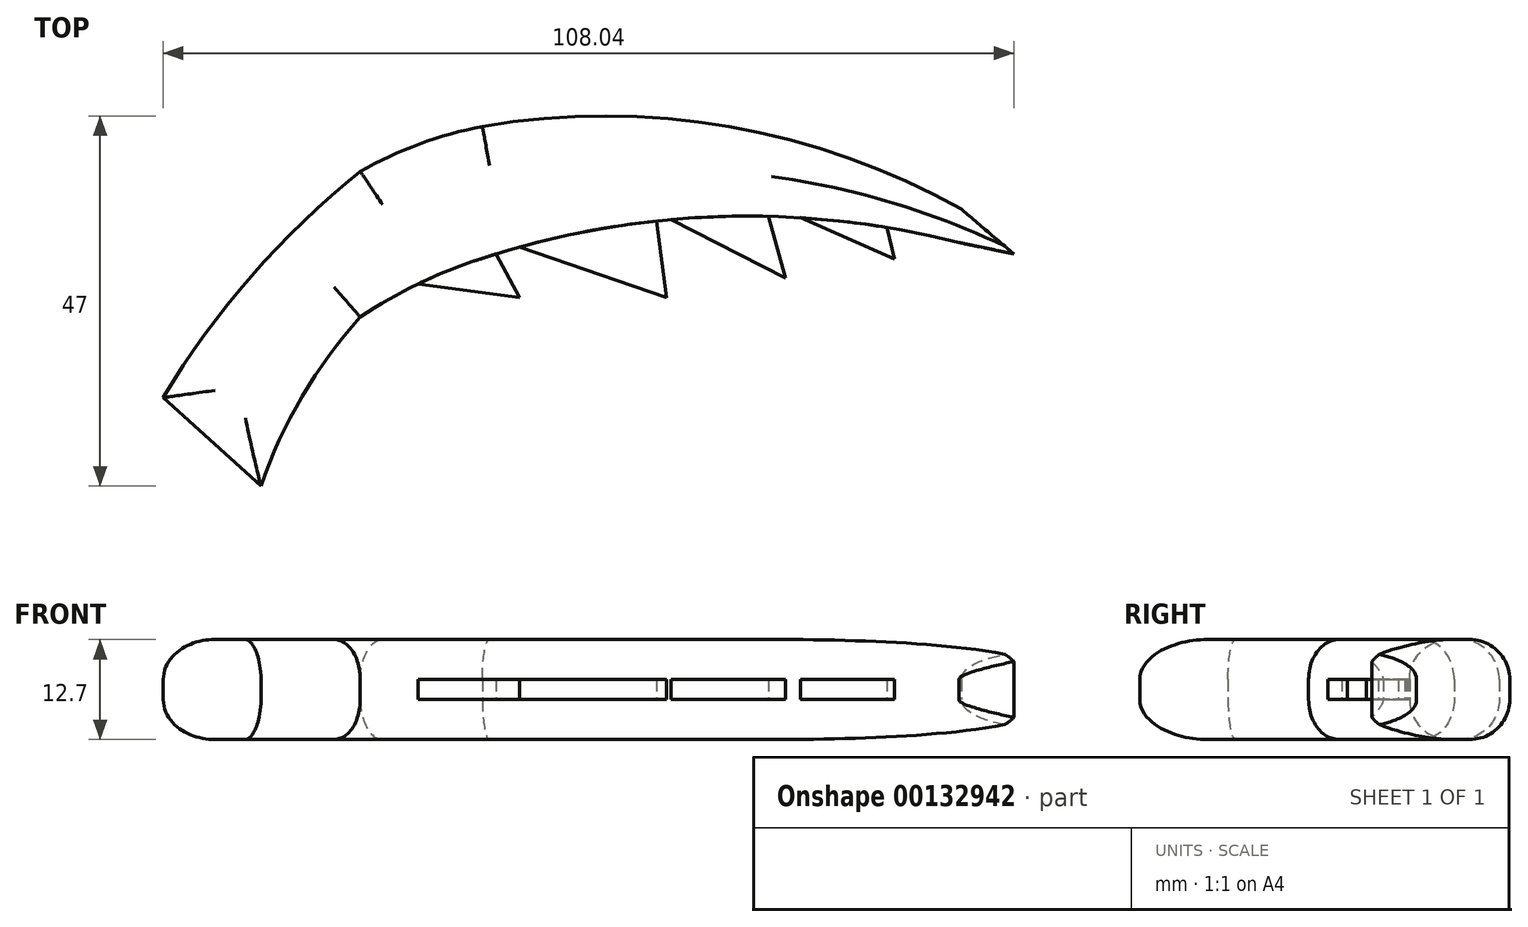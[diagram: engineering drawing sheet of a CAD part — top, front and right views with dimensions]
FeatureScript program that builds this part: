
annotation { "Feature Type Name" : "Feature", "Feature Type Description" : "" }
export const myFeature = defineFeature(function(context is Context, id is Id, definition is map)
    precondition{}
    {
        {
            var Q0;
            Q0=qCreatedBy(makeId("Top.planeOp"),FACE);
            var sketch = newSketch(context, id + "F0", { "sketchPlane" : qUnion([Q0])});
            skLineSegment(sketch, "E0", {"start": v(-49.45, -53.5) * mm, "end": v(-61.87, -42.29) * mm});
            skPoint(sketch, "E1", {"position": v(46.17, -24.01) * mm});
            skPoint(sketch, "E2", {"position": v(39.2, -22.57) * mm});
            skArc(sketch, "E3", {"start": v(39.2, -22.57) * mm, "mid": v(8.62, -19.28) * mm, "end": v(-21.66, -24.68) * mm});
            skPoint(sketch, "E4", {"position": v(39.51, -18.33) * mm});
            skArc(sketch, "E5", {"start": v(39.51, -18.33) * mm, "mid": v(10, -7.85) * mm, "end": v(-21.33, -7.82) * mm});
            skLineSegment(sketch, "E6", {"start": v(39.51, -18.33) * mm, "end": v(46.17, -24.01) * mm});
            skLineSegment(sketch, "E7", {"start": v(39.2, -22.57) * mm, "end": v(46.17, -24.01) * mm});
            skPoint(sketch, "E8", {"position": v(-36.84, -13.55) * mm});
            skArc(sketch, "E9", {"start": v(-36.84, -13.55) * mm, "mid": v(-50.64, -26.8) * mm, "end": v(-61.87, -42.29) * mm});
            skArc(sketch, "E10", {"start": v(-21.33, -7.82) * mm, "mid": v(-29.32, -10.05) * mm, "end": v(-36.84, -13.55) * mm});
            skPoint(sketch, "E11", {"position": v(-36.84, -32.06) * mm});
            skArc(sketch, "E12", {"start": v(-36.84, -32.06) * mm, "mid": v(-44.23, -42.14) * mm, "end": v(-49.45, -53.5) * mm});
            skArc(sketch, "E13", {"start": v(-21.66, -24.68) * mm, "mid": v(-29.5, -27.84) * mm, "end": v(-36.84, -32.06) * mm});
            skSolve(sketch);
        }
        {
            var Q0;
            Q0=makeQuery(id+"F0.imprint","IMPRINT",FACE,{"disambiguationData":[TD([[makeQuery(id+"F0.imprint","IMPRINT",EDGE,{"derivedFrom":sQuery(id+"F0.wireOp",EDGE,"E0")}),-1.0]])]});
            extrude(context, id + "F1", {"entities" : qUnion([Q0]), "depth" : 12.7 * mm});
        }
        {
            var Q0;
            Q0=makeQuery(id+"F1.opExtrude","CAP_FACE",FACE,{"disambiguationData":[OSD([sQuery(id+"F0.wireOp",EDGE,"E0"),sQuery(id+"F0.wireOp",EDGE,"E3"),sQuery(id+"F0.wireOp",EDGE,"E5"),sQuery(id+"F0.wireOp",EDGE,"E6"),sQuery(id+"F0.wireOp",EDGE,"E7"),sQuery(id+"F0.wireOp",EDGE,"E9"),sQuery(id+"F0.wireOp",EDGE,"E10"),sQuery(id+"F0.wireOp",EDGE,"E12"),sQuery(id+"F0.wireOp",EDGE,"E13")])],"isStart":false});
            var Q1;
            Q1=makeQuery(id+"F1.opExtrude","CAP_FACE",FACE,{"disambiguationData":[OSD([sQuery(id+"F0.wireOp",EDGE,"E0"),sQuery(id+"F0.wireOp",EDGE,"E3"),sQuery(id+"F0.wireOp",EDGE,"E5"),sQuery(id+"F0.wireOp",EDGE,"E6"),sQuery(id+"F0.wireOp",EDGE,"E7"),sQuery(id+"F0.wireOp",EDGE,"E9"),sQuery(id+"F0.wireOp",EDGE,"E10"),sQuery(id+"F0.wireOp",EDGE,"E12"),sQuery(id+"F0.wireOp",EDGE,"E13")])],"isStart":true});
            fillet(context, id + "F2", {"entities" : qUnion([Q0, Q1]), "radius" : 5.08 * mm, "tangentPropagation" : true, "allowEdgeOverflow" : false});
        }
        {
            var Q0;
            Q0=qCreatedBy(makeId("Top.planeOp"),FACE);
            cPlane(context, id + "F3", {"entities" : qUnion([Q0]), "cplaneType" : CPlaneType.OFFSET, "offset" : 6.35 * mm, "width" : 152.4 * mm, "height" : 152.4 * mm});
        }
        {
            var Q0;
            Q0=qCreatedBy(id+"F3.planeOp",FACE);
            var sketch = newSketch(context, id + "F4", { "sketchPlane" : qUnion([Q0])});
            skLineSegment(sketch, "E14.0.0", {"start": v(-61.87, -42.29) * mm, "end": v(-49.45, -53.5) * mm});
            skArc(sketch, "E14.0.1", {"start": v(-49.45, -53.5) * mm, "mid": v(-44.23, -42.14) * mm, "end": v(-36.84, -32.06) * mm});
            skArc(sketch, "E14.0.2", {"start": v(-36.84, -32.06) * mm, "mid": v(-29.5, -27.84) * mm, "end": v(-21.66, -24.68) * mm});
            skArc(sketch, "E14.0.3", {"start": v(-21.66, -24.68) * mm, "mid": v(8.62, -19.28) * mm, "end": v(39.2, -22.57) * mm});
            skLineSegment(sketch, "E14.0.4", {"start": v(39.2, -22.57) * mm, "end": v(46.17, -24.01) * mm});
            skLineSegment(sketch, "E14.0.5", {"start": v(46.17, -24.01) * mm, "end": v(39.51, -18.33) * mm});
            skArc(sketch, "E14.0.6", {"start": v(39.51, -18.33) * mm, "mid": v(10, -7.85) * mm, "end": v(-21.33, -7.82) * mm});
            skArc(sketch, "E14.0.7", {"start": v(-21.33, -7.82) * mm, "mid": v(-29.32, -10.05) * mm, "end": v(-36.84, -13.55) * mm});
            skArc(sketch, "E14.0.8", {"start": v(-36.84, -13.55) * mm, "mid": v(-50.64, -26.8) * mm, "end": v(-61.87, -42.29) * mm});
            skLineSegment(sketch, "E15", {"start": v(-29.5, -27.84) * mm, "end": v(-16.64, -29.58) * mm});
            skLineSegment(sketch, "E16", {"start": v(-16.64, -29.58) * mm, "end": v(-19.6, -24.02) * mm});
            skLineSegment(sketch, "E17", {"start": v(-16.64, -23.16) * mm, "end": v(2.04, -29.58) * mm});
            skLineSegment(sketch, "E18", {"start": v(2.62, -19.66) * mm, "end": v(17.15, -27.1) * mm});
            skLineSegment(sketch, "E19", {"start": v(19.07, -19.42) * mm, "end": v(31.04, -24.68) * mm});
            skLineSegment(sketch, "E20", {"start": v(31.04, -24.68) * mm, "end": v(30.09, -20.67) * mm});
            skLineSegment(sketch, "E21", {"start": v(17.15, -27.1) * mm, "end": v(15.01, -19.25) * mm});
            skLineSegment(sketch, "E22", {"start": v(2.04, -29.58) * mm, "end": v(0.81, -19.84) * mm});
            skSolve(sketch);
        }
        {
            var Q0;
            {var subQ0=sQuery(id+"F4.wireOp",EDGE,"E17");Q0=makeQuery(id+"F4.imprint","IMPRINT",FACE,{"disambiguationData":[TD([[makeQuery(id+"F4.imprint","IMPRINT",EDGE,{"derivedFrom":subQ0}),1.0]])]});}
            var Q1;
            {var subQ3=sQuery(id+"F4.wireOp",EDGE,"E15");Q1=makeQuery(id+"F4.imprint","IMPRINT",FACE,{"disambiguationData":[TD([[makeQuery(id+"F4.imprint","IMPRINT",EDGE,{"derivedFrom":subQ3}),1.0]])]});}
            var Q2;
            {var subQ0=sQuery(id+"F4.wireOp",EDGE,"E19");Q2=makeQuery(id+"F4.imprint","IMPRINT",FACE,{"disambiguationData":[TD([[makeQuery(id+"F4.imprint","IMPRINT",EDGE,{"derivedFrom":subQ0}),1.0]])]});}
            var Q3;
            {var subQ0=sQuery(id+"F4.wireOp",EDGE,"E18");Q3=makeQuery(id+"F4.imprint","IMPRINT",FACE,{"disambiguationData":[TD([[makeQuery(id+"F4.imprint","IMPRINT",EDGE,{"derivedFrom":subQ0}),1.0]])]});}
            extrude(context, id + "F5", {"entities" : qUnion([Q0, Q1, Q2, Q3]), "endBound" : BoundingType.SYMMETRIC, "depth" : 2.54 * mm});
        }
    });
